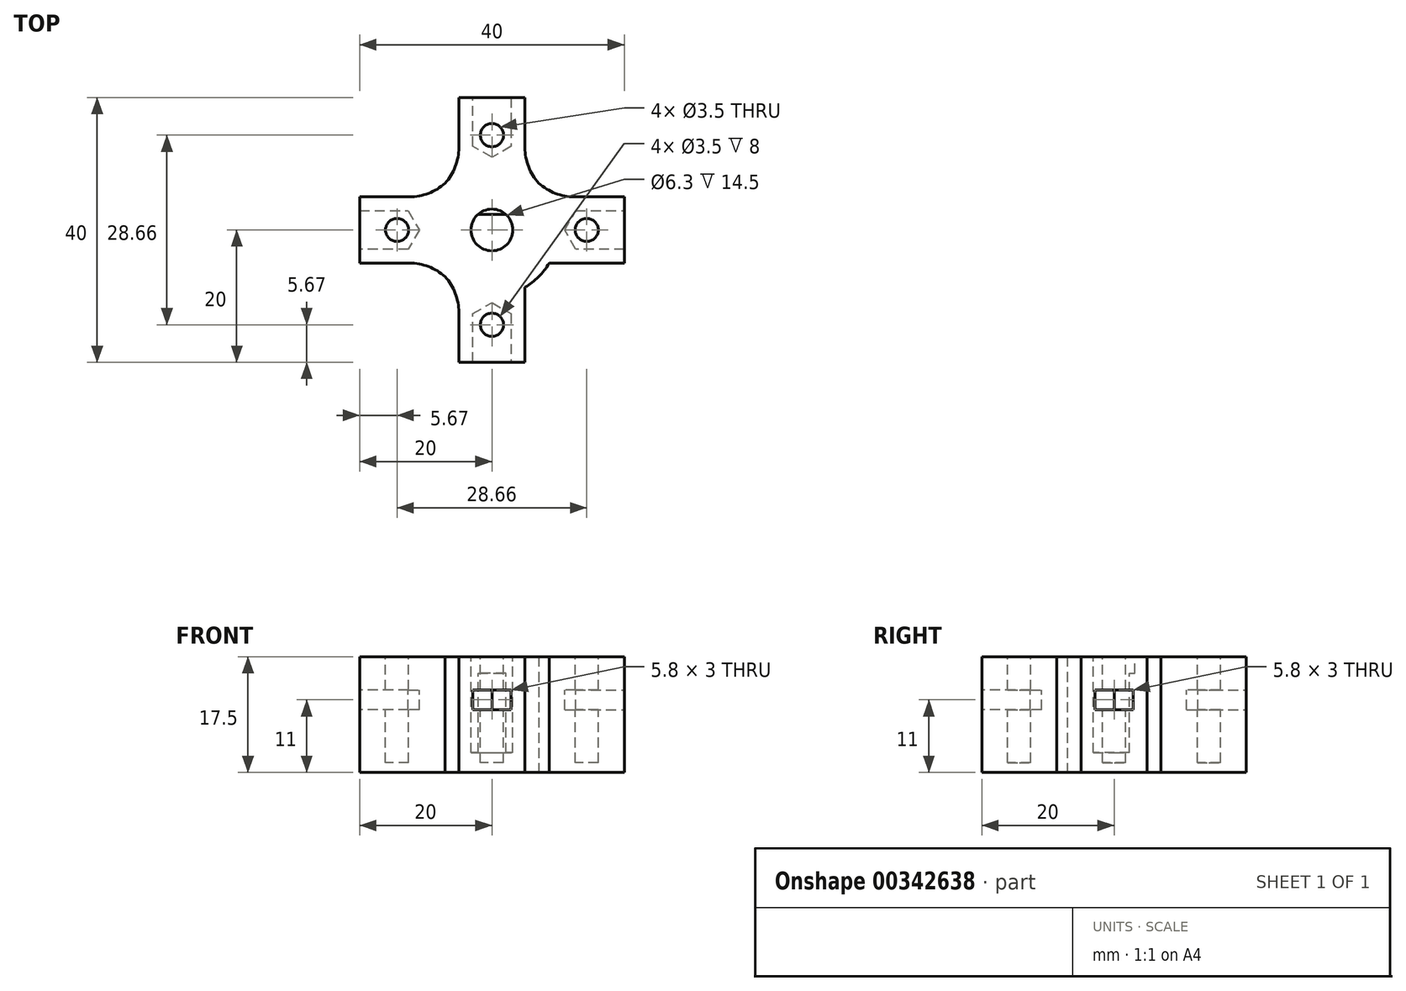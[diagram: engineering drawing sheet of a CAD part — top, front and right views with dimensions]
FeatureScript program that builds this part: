
annotation { "Feature Type Name" : "Feature", "Feature Type Description" : "" }
export const myFeature = defineFeature(function(context is Context, id is Id, definition is map)
    precondition{}
    {
        {
            var Q0;
            Q0=qCreatedBy(makeId("Top.planeOp"),FACE);
            var sketch = newSketch(context, id + "F0", { "sketchPlane" : qUnion([Q0])});
            skCircle(sketch, "E0", {"center": v(0, 0) * mm, "radius": 5 * mm});
            skSolve(sketch);
        }
        {
            var Q0;
            Q0=qSketchRegion(id+"F0",true);
            extrude(context, id + "F1", {"entities" : qUnion([Q0]), "depth" : 15 * mm});
        }
        {
            var Q0;
            Q0=makeQuery(id+"F1.opExtrude","CAP_FACE",FACE,{"disambiguationData":[OSD([sQuery(id+"F0.wireOp",EDGE,"E0")])],"isStart":false});
            var sketch = newSketch(context, id + "F2", { "sketchPlane" : qUnion([Q0])});
            skArc(sketch, "E1", {"start": v(-2.1, 2.35) * mm, "mid": v(0, -3.15) * mm, "end": v(2.1, 2.35) * mm});
            skLineSegment(sketch, "E2", {"start": v(-2.1, 2.35) * mm, "end": v(2.1, 2.35) * mm});
            skSolve(sketch);
        }
        {
            var Q0;
            Q0=qSketchRegion(id+"F2",true);
            extrude(context, id + "F3", {"entities" : qUnion([Q0]), "operationType" : NewBodyOperationType.REMOVE, "oppositeDirection" : true, "depth" : 12 * mm});
        }
        {
            var Q0;
            Q0=makeQuery(id+"F1.opExtrude","CAP_FACE",FACE,{"disambiguationData":[OSD([sQuery(id+"F0.wireOp",EDGE,"E0")])],"isStart":true});
            chamfer(context, id + "F4", {"entities" : qUnion([Q0]), "width" : 0.3 * mm, "tangentPropagation" : true});
        }
        {
            var Q0;
            Q0=makeQuery(id+"F1.opExtrude","CAP_FACE",FACE,{"disambiguationData":[OSD([sQuery(id+"F0.wireOp",EDGE,"E0")])],"isStart":false});
            var sketch = newSketch(context, id + "F5", { "sketchPlane" : qUnion([Q0])});
            skArc(sketch, "E3.0", {"start": v(-2.1, 2.35) * mm, "mid": v(0, -3.15) * mm, "end": v(2.1, 2.35) * mm, "construction": true});
            skCircle(sketch, "E4.0", {"center": v(0, 0) * mm, "radius": 5 * mm});
            skCircle(sketch, "E5", {"center": v(0, 0) * mm, "radius": 3.15 * mm});
            skSolve(sketch);
        }
        {
            var Q0;
            Q0 = qSketchRegion(id + "F5", true);
            extrude(context, id + "F6", {"entities" : qUnion([Q0]), "operationType" : NewBodyOperationType.ADD, "depth" : 2.5 * mm});
        }
        {
            var Q0;
            Q0=qCreatedBy(makeId("Top.planeOp"),FACE);
            var sketch = newSketch(context, id + "F7", { "sketchPlane" : qUnion([Q0])});
            skCircle(sketch, "E6", {"center": v(0, 0) * mm, "radius": 7 * mm, "construction": true});
            skCircle(sketch, "E7", {"center": v(0, 0) * mm, "radius": 10 * mm});
            skCircle(sketch, "E8.0", {"center": v(0, 0) * mm, "radius": 3.15 * mm});
            skSolve(sketch);
        }
        {
            var Q0;
            Q0 = qSketchRegion(id + "F7", true);
            var Q1;
            Q1=makeQuery(id+"F6.opExtrude","CAP_FACE",FACE,{"disambiguationData":[OSD([sQuery(id+"F5.wireOp",EDGE,"E4.0"),sQuery(id+"F5.wireOp",EDGE,"E5")])],"isStart":false});
            extrude(context, id + "F8", {"entities" : qUnion([Q0]), "operationType" : NewBodyOperationType.ADD, "endBound" : BoundingType.UP_TO_SURFACE, "endBoundEntityFace" : qUnion([Q1]), "depth" : 25 * mm});
        }
        {
            var Q0;
            Q0=makeQuery(id+"F8.boolean.opBoolean","MERGE",FACE,{"derivedFrom":[makeQuery(id+"F1.opExtrude","CAP_FACE",FACE,{"disambiguationData":[OSD([sQuery(id+"F0.wireOp",EDGE,"E0")])],"isStart":true}),makeQuery(id+"F8.opExtrude","CAP_FACE",FACE,{"disambiguationData":[OSD([sQuery(id+"F7.wireOp",EDGE,"E7"),sQuery(id+"F7.wireOp",EDGE,"E8.0")])],"isStart":true})]});
            var sketch = newSketch(context, id + "F9", { "sketchPlane" : qUnion([Q0])});
            skArc(sketch, "E9.0", {"start": v(8.66, -5) * mm, "mid": v(10, 0) * mm, "end": v(8.66, 5) * mm});
            skLineSegment(sketch, "E10", {"start": v(8.66, -5) * mm, "end": v(20, -5) * mm});
            skLineSegment(sketch, "E11", {"start": v(8.66, 5) * mm, "end": v(20, 5) * mm});
            skLineSegment(sketch, "E12", {"start": v(20, -5) * mm, "end": v(20, 5) * mm});
            skPoint(sketch, "E13", {"position": v(14.33, 0) * mm});
            skPoint(sketch, "E13.positionSnap0", {"position": v(14.33, -5) * mm});
            skPoint(sketch, "E14.1.0", {"position": v(5, 14.33) * mm});
            skPoint(sketch, "E14.1.1", {"position": v(0, 14.33) * mm});
            skLineSegment(sketch, "E14.1.2", {"start": v(5, 20) * mm, "end": v(-5, 20) * mm});
            skLineSegment(sketch, "E14.1.3", {"start": v(-5, 8.66) * mm, "end": v(-5, 20) * mm});
            skLineSegment(sketch, "E14.1.4", {"start": v(5, 8.66) * mm, "end": v(5, 20) * mm});
            skArc(sketch, "E14.1.5", {"start": v(5, 8.66) * mm, "mid": v(0, 10) * mm, "end": v(-5, 8.66) * mm});
            skPoint(sketch, "E14.2.0", {"position": v(-14.33, 5) * mm});
            skPoint(sketch, "E14.2.1", {"position": v(-14.33, 0) * mm});
            skLineSegment(sketch, "E14.2.2", {"start": v(-20, 5) * mm, "end": v(-20, -5) * mm});
            skLineSegment(sketch, "E14.2.3", {"start": v(-8.66, -5) * mm, "end": v(-20, -5) * mm});
            skLineSegment(sketch, "E14.2.4", {"start": v(-8.66, 5) * mm, "end": v(-20, 5) * mm});
            skArc(sketch, "E14.2.5", {"start": v(-8.66, 5) * mm, "mid": v(-10, 0) * mm, "end": v(-8.66, -5) * mm});
            skPoint(sketch, "E14.3.0", {"position": v(-5, -14.33) * mm});
            skPoint(sketch, "E14.3.1", {"position": v(0, -14.33) * mm});
            skLineSegment(sketch, "E14.3.2", {"start": v(-5, -20) * mm, "end": v(5, -20) * mm});
            skLineSegment(sketch, "E14.3.3", {"start": v(5, -8.66) * mm, "end": v(5, -20) * mm});
            skLineSegment(sketch, "E14.3.4", {"start": v(-5, -8.66) * mm, "end": v(-5, -20) * mm});
            skArc(sketch, "E14.3.5", {"start": v(-5, -8.66) * mm, "mid": v(0, -10) * mm, "end": v(5, -8.66) * mm});
            skLineSegment(sketch, "E14.anchor1", {"start": v(0, 0) * mm, "end": v(8.66, -5) * mm, "construction": true});
            skLineSegment(sketch, "E14.anchor2", {"start": v(0, 0) * mm, "end": v(-5, -8.66) * mm, "construction": true});
            skSolve(sketch);
        }
        {
            var Q0;
            Q0 = qSketchRegion(id + "F9", true);
            var Q1;
            {var subQ0=sQuery(id+"F5.wireOp",EDGE,"E5");var subQ1=sQuery(id+"F5.wireOp",EDGE,"E4.0");Q1=makeQuery(id+"F8.boolean.opBoolean","MERGE",FACE,{"derivedFrom":[makeQuery(id+"F6.opExtrude","CAP_FACE",FACE,{"disambiguationData":[OSD([subQ1,subQ0])],"isStart":false}),makeQuery(id+"F8.opExtrude","CAP_FACE",FACE,{"disambiguationData":[OSD([subQ1,subQ0])],"isStart":false})]});}
            extrude(context, id + "F10", {"entities" : qUnion([Q0]), "operationType" : NewBodyOperationType.ADD, "endBound" : BoundingType.UP_TO_SURFACE, "oppositeDirection" : true, "endBoundEntityFace" : qUnion([Q1]), "depth" : 25 * mm});
        }
        {
            var Q0;
            {var subQ0=sQuery(id+"F5.wireOp",EDGE,"E5");var subQ1=sQuery(id+"F5.wireOp",EDGE,"E4.0");Q0=makeQuery(id+"F10.boolean.opBoolean","MERGE",FACE,{"derivedFrom":[makeQuery(id+"F8.boolean.opBoolean","MERGE",FACE,{"derivedFrom":[makeQuery(id+"F6.opExtrude","CAP_FACE",FACE,{"disambiguationData":[OSD([subQ1,subQ0])],"isStart":false}),makeQuery(id+"F8.opExtrude","CAP_FACE",FACE,{"disambiguationData":[OSD([subQ1,subQ0])],"isStart":false})]}),makeQuery(id+"F10.opExtrude","CAP_FACE",FACE,{"disambiguationData":[OSD([subQ1,subQ0]),ownerDisambiguation([makeQuery(id+"F9.imprint","IMPRINT",EDGE,{"derivedFrom":sQuery(id+"F9.wireOp",EDGE,"E9.0")})])],"isStart":false}),makeQuery(id+"F10.opExtrude","CAP_FACE",FACE,{"disambiguationData":[OSD([subQ1,subQ0]),ownerDisambiguation([makeQuery(id+"F9.imprint","IMPRINT",EDGE,{"derivedFrom":sQuery(id+"F9.wireOp",EDGE,"E14.1.2")})])],"isStart":false}),makeQuery(id+"F10.opExtrude","CAP_FACE",FACE,{"disambiguationData":[OSD([subQ1,subQ0]),ownerDisambiguation([makeQuery(id+"F9.imprint","IMPRINT",EDGE,{"derivedFrom":sQuery(id+"F9.wireOp",EDGE,"E14.2.2")})])],"isStart":false}),makeQuery(id+"F10.opExtrude","CAP_FACE",FACE,{"disambiguationData":[OSD([subQ1,subQ0]),ownerDisambiguation([makeQuery(id+"F9.imprint","IMPRINT",EDGE,{"derivedFrom":sQuery(id+"F9.wireOp",EDGE,"E14.3.2")})])],"isStart":false})]});}
            var sketch = newSketch(context, id + "F11", { "sketchPlane" : qUnion([Q0])});
            skCircle(sketch, "E15", {"center": v(14.33, 0) * mm, "radius": 1.75 * mm});
            skCircle(sketch, "E16.1.0", {"center": v(0, 14.33) * mm, "radius": 1.75 * mm});
            skCircle(sketch, "E16.2.0", {"center": v(-14.33, 0) * mm, "radius": 1.75 * mm});
            skCircle(sketch, "E16.3.0", {"center": v(0, -14.33) * mm, "radius": 1.75 * mm});
            skPoint(sketch, "E16.center", {"position": v(0, 0) * mm});
            skSolve(sketch);
        }
        {
            var Q0;
            Q0 = qSketchRegion(id + "F11", true);
            extrude(context, id + "F12", {"entities" : qUnion([Q0]), "operationType" : NewBodyOperationType.REMOVE, "oppositeDirection" : true, "depth" : 16 * mm});
        }
        {
            var Q0;
            {var subQ0=sQuery(id+"F5.wireOp",EDGE,"E5");var subQ1=sQuery(id+"F5.wireOp",EDGE,"E4.0");Q0=makeQuery(id+"F10.boolean.opBoolean","MERGE",FACE,{"derivedFrom":[makeQuery(id+"F8.boolean.opBoolean","MERGE",FACE,{"derivedFrom":[makeQuery(id+"F6.opExtrude","CAP_FACE",FACE,{"disambiguationData":[OSD([subQ1,subQ0])],"isStart":false}),makeQuery(id+"F8.opExtrude","CAP_FACE",FACE,{"disambiguationData":[OSD([subQ1,subQ0])],"isStart":false})]}),makeQuery(id+"F10.opExtrude","CAP_FACE",FACE,{"disambiguationData":[OSD([subQ1,subQ0]),ownerDisambiguation([makeQuery(id+"F9.imprint","IMPRINT",EDGE,{"derivedFrom":sQuery(id+"F9.wireOp",EDGE,"E9.0")})])],"isStart":false}),makeQuery(id+"F10.opExtrude","CAP_FACE",FACE,{"disambiguationData":[OSD([subQ1,subQ0]),ownerDisambiguation([makeQuery(id+"F9.imprint","IMPRINT",EDGE,{"derivedFrom":sQuery(id+"F9.wireOp",EDGE,"E14.1.2")})])],"isStart":false}),makeQuery(id+"F10.opExtrude","CAP_FACE",FACE,{"disambiguationData":[OSD([subQ1,subQ0]),ownerDisambiguation([makeQuery(id+"F9.imprint","IMPRINT",EDGE,{"derivedFrom":sQuery(id+"F9.wireOp",EDGE,"E14.2.2")})])],"isStart":false}),makeQuery(id+"F10.opExtrude","CAP_FACE",FACE,{"disambiguationData":[OSD([subQ1,subQ0]),ownerDisambiguation([makeQuery(id+"F9.imprint","IMPRINT",EDGE,{"derivedFrom":sQuery(id+"F9.wireOp",EDGE,"E14.3.2")})])],"isStart":false})]});}
            var sketch = newSketch(context, id + "F13", { "sketchPlane" : qUnion([Q0])});
            skCircle(sketch, "E17.0", {"center": v(14.33, 0) * mm, "radius": 1.75 * mm, "construction": true});
            skCircle(sketch, "E18.cCircle", {"center": v(14.33, 0) * mm, "radius": 2.9 * mm, "construction": true});
            skLineSegment(sketch, "E18.0", {"start": v(12.66, 2.9) * mm, "end": v(16, 2.9) * mm});
            skLineSegment(sketch, "E18.1", {"start": v(16, 2.9) * mm, "end": v(17.68, 0) * mm, "construction": true});
            skLineSegment(sketch, "E18.2", {"start": v(17.68, 0) * mm, "end": v(16, -2.9) * mm, "construction": true});
            skLineSegment(sketch, "E18.3", {"start": v(16, -2.9) * mm, "end": v(12.66, -2.9) * mm});
            skLineSegment(sketch, "E18.4", {"start": v(12.66, -2.9) * mm, "end": v(10.98, 0) * mm});
            skLineSegment(sketch, "E18.5", {"start": v(10.98, 0) * mm, "end": v(12.66, 2.9) * mm});
            skPoint(sketch, "E18.0.midPoint", {"position": v(14.33, 2.9) * mm});
            skLineSegment(sketch, "E19", {"start": v(16, 2.9) * mm, "end": v(20, 2.9) * mm});
            skLineSegment(sketch, "E20", {"start": v(20, 2.9) * mm, "end": v(20, -2.9) * mm});
            skLineSegment(sketch, "E21", {"start": v(20, -2.9) * mm, "end": v(16, -2.9) * mm});
            skLineSegment(sketch, "E22.1.0", {"start": v(-2.9, 12.66) * mm, "end": v(-2.9, 16) * mm});
            skLineSegment(sketch, "E22.1.1", {"start": v(-2.9, 16) * mm, "end": v(0, 17.68) * mm, "construction": true});
            skLineSegment(sketch, "E22.1.2", {"start": v(0, 17.68) * mm, "end": v(2.9, 16) * mm, "construction": true});
            skLineSegment(sketch, "E22.1.3", {"start": v(2.9, 16) * mm, "end": v(2.9, 12.66) * mm});
            skLineSegment(sketch, "E22.1.4", {"start": v(2.9, 12.66) * mm, "end": v(0, 10.98) * mm});
            skLineSegment(sketch, "E22.1.5", {"start": v(0, 10.98) * mm, "end": v(-2.9, 12.66) * mm});
            skLineSegment(sketch, "E22.1.6", {"start": v(-2.9, 16) * mm, "end": v(-2.9, 20) * mm});
            skLineSegment(sketch, "E22.1.7", {"start": v(-2.9, 20) * mm, "end": v(2.9, 20) * mm});
            skLineSegment(sketch, "E22.1.8", {"start": v(2.9, 20) * mm, "end": v(2.9, 16) * mm});
            skPoint(sketch, "E22.1.9", {"position": v(-2.9, 14.33) * mm});
            skCircle(sketch, "E22.1.10", {"center": v(0, 14.33) * mm, "radius": 2.9 * mm, "construction": true});
            skCircle(sketch, "E22.1.11", {"center": v(0, 14.33) * mm, "radius": 1.75 * mm, "construction": true});
            skLineSegment(sketch, "E22.2.0", {"start": v(-12.66, -2.9) * mm, "end": v(-16, -2.9) * mm});
            skLineSegment(sketch, "E22.2.1", {"start": v(-16, -2.9) * mm, "end": v(-17.68, 0) * mm, "construction": true});
            skLineSegment(sketch, "E22.2.2", {"start": v(-17.68, 0) * mm, "end": v(-16, 2.9) * mm, "construction": true});
            skLineSegment(sketch, "E22.2.3", {"start": v(-16, 2.9) * mm, "end": v(-12.66, 2.9) * mm});
            skLineSegment(sketch, "E22.2.4", {"start": v(-12.66, 2.9) * mm, "end": v(-10.98, 0) * mm});
            skLineSegment(sketch, "E22.2.5", {"start": v(-10.98, 0) * mm, "end": v(-12.66, -2.9) * mm});
            skLineSegment(sketch, "E22.2.6", {"start": v(-16, -2.9) * mm, "end": v(-20, -2.9) * mm});
            skLineSegment(sketch, "E22.2.7", {"start": v(-20, -2.9) * mm, "end": v(-20, 2.9) * mm});
            skLineSegment(sketch, "E22.2.8", {"start": v(-20, 2.9) * mm, "end": v(-16, 2.9) * mm});
            skPoint(sketch, "E22.2.9", {"position": v(-14.33, -2.9) * mm});
            skCircle(sketch, "E22.2.10", {"center": v(-14.33, 0) * mm, "radius": 2.9 * mm, "construction": true});
            skCircle(sketch, "E22.2.11", {"center": v(-14.33, 0) * mm, "radius": 1.75 * mm, "construction": true});
            skLineSegment(sketch, "E22.3.0", {"start": v(2.9, -12.66) * mm, "end": v(2.9, -16) * mm});
            skLineSegment(sketch, "E22.3.1", {"start": v(2.9, -16) * mm, "end": v(0, -17.68) * mm, "construction": true});
            skLineSegment(sketch, "E22.3.2", {"start": v(0, -17.68) * mm, "end": v(-2.9, -16) * mm, "construction": true});
            skLineSegment(sketch, "E22.3.3", {"start": v(-2.9, -16) * mm, "end": v(-2.9, -12.66) * mm});
            skLineSegment(sketch, "E22.3.4", {"start": v(-2.9, -12.66) * mm, "end": v(0, -10.98) * mm});
            skLineSegment(sketch, "E22.3.5", {"start": v(0, -10.98) * mm, "end": v(2.9, -12.66) * mm});
            skLineSegment(sketch, "E22.3.6", {"start": v(2.9, -16) * mm, "end": v(2.9, -20) * mm});
            skLineSegment(sketch, "E22.3.7", {"start": v(2.9, -20) * mm, "end": v(-2.9, -20) * mm});
            skLineSegment(sketch, "E22.3.8", {"start": v(-2.9, -20) * mm, "end": v(-2.9, -16) * mm});
            skPoint(sketch, "E22.3.9", {"position": v(2.9, -14.33) * mm});
            skCircle(sketch, "E22.3.10", {"center": v(0, -14.33) * mm, "radius": 2.9 * mm, "construction": true});
            skCircle(sketch, "E22.3.11", {"center": v(0, -14.33) * mm, "radius": 1.75 * mm, "construction": true});
            skPoint(sketch, "E22.center", {"position": v(0, 0) * mm});
            skSolve(sketch);
        }
        {
            var Q0;
            Q0 = qSketchRegion(id + "F13", true);
            extrude(context, id + "F14", {"entities" : qUnion([Q0]), "operationType" : NewBodyOperationType.REMOVE, "oppositeDirection" : true, "depth" : 8 * mm, "hasSecondDirection" : true, "secondDirectionOppositeDirection" : true, "secondDirectionDepth" : 5 * mm});
        }
        {
            var Q0;
            Q0=makeQuery(id+"F10.opExtrude","SWEPT_EDGE",EDGE,{"disambiguationData":[OSD([sQuery(id+"F7.wireOp",EDGE,"E7"),sQuery(id+"F9.wireOp",EDGE,"E14.1.4"),sQuery(id+"F9.wireOp",EDGE,"E14.1.5")])]});
            var Q1;
            Q1=makeQuery(id+"F10.opExtrude","SWEPT_EDGE",EDGE,{"disambiguationData":[OSD([sQuery(id+"F7.wireOp",EDGE,"E7"),sQuery(id+"F9.wireOp",EDGE,"E9.0"),sQuery(id+"F9.wireOp",EDGE,"E11")])]});
            var Q2;
            Q2=makeQuery(id+"F10.opExtrude","SWEPT_EDGE",EDGE,{"disambiguationData":[OSD([sQuery(id+"F7.wireOp",EDGE,"E7"),sQuery(id+"F9.wireOp",EDGE,"E14.2.4"),sQuery(id+"F9.wireOp",EDGE,"E14.2.5")])]});
            var Q3;
            Q3=makeQuery(id+"F10.opExtrude","SWEPT_EDGE",EDGE,{"disambiguationData":[OSD([sQuery(id+"F7.wireOp",EDGE,"E7"),sQuery(id+"F9.wireOp",EDGE,"E14.1.3"),sQuery(id+"F9.wireOp",EDGE,"E14.1.5")])]});
            var Q4;
            Q4=makeQuery(id+"F10.opExtrude","SWEPT_EDGE",EDGE,{"disambiguationData":[OSD([sQuery(id+"F7.wireOp",EDGE,"E7"),sQuery(id+"F9.wireOp",EDGE,"E14.2.3"),sQuery(id+"F9.wireOp",EDGE,"E14.2.5")])]});
            var Q5;
            Q5=makeQuery(id+"F10.opExtrude","SWEPT_EDGE",EDGE,{"disambiguationData":[OSD([sQuery(id+"F7.wireOp",EDGE,"E7"),sQuery(id+"F9.wireOp",EDGE,"E14.3.4"),sQuery(id+"F9.wireOp",EDGE,"E14.3.5")])]});
            var Q6;
            Q6=makeQuery(id+"F10.opExtrude","SWEPT_EDGE",EDGE,{"disambiguationData":[OSD([sQuery(id+"F7.wireOp",EDGE,"E7"),sQuery(id+"F9.wireOp",EDGE,"E14.3.3"),sQuery(id+"F9.wireOp",EDGE,"E14.3.5")])]});
            var Q7;
            Q7=makeQuery(id+"F10.opExtrude","SWEPT_EDGE",EDGE,{"disambiguationData":[OSD([sQuery(id+"F7.wireOp",EDGE,"E7"),sQuery(id+"F9.wireOp",EDGE,"E9.0"),sQuery(id+"F9.wireOp",EDGE,"E10")])]});
            fillet(context, id + "F15", {"entities" : qUnion([Q0, Q1, Q2, Q3, Q4, Q5, Q6, Q7]), "radius" : 8 * mm, "tangentPropagation" : true, "allowEdgeOverflow" : false});
        }
    });
